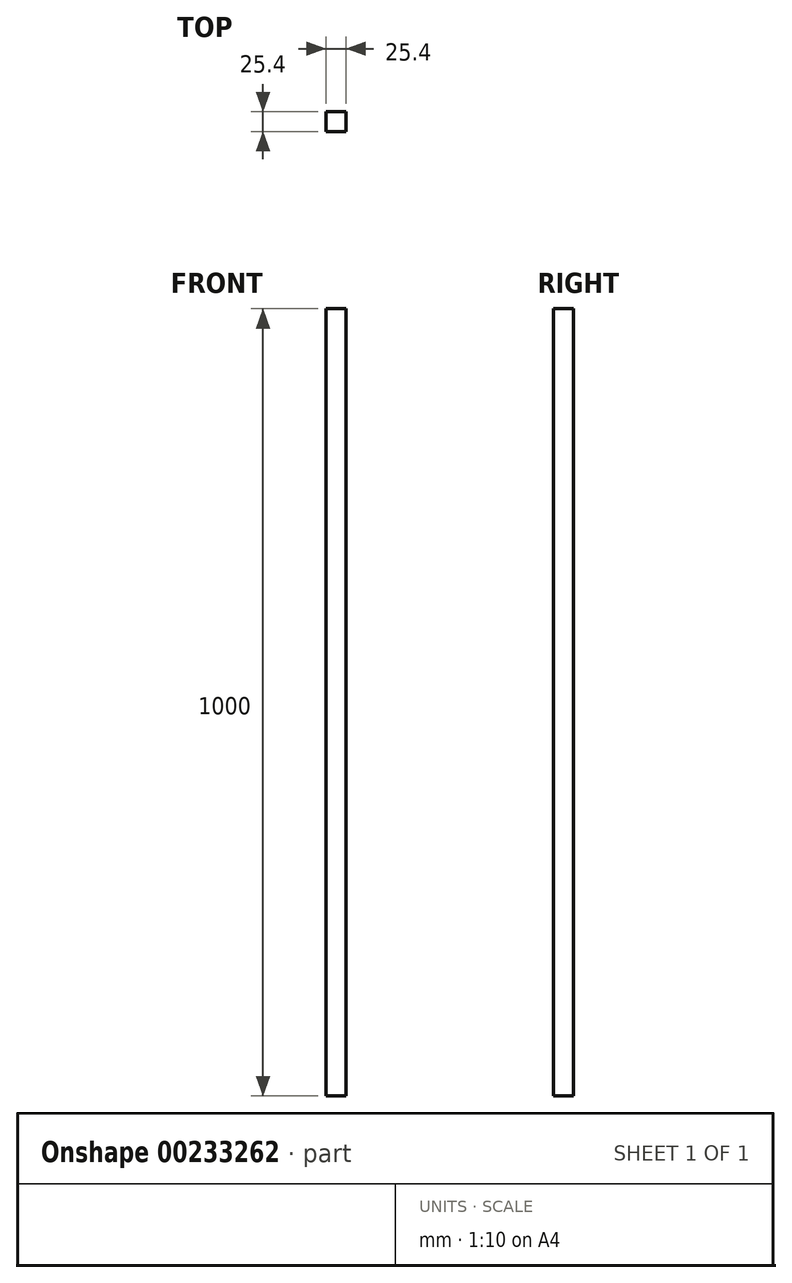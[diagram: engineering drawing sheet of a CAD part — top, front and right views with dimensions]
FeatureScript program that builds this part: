
annotation { "Feature Type Name" : "Feature", "Feature Type Description" : "" }
export const myFeature = defineFeature(function(context is Context, id is Id, definition is map)
    precondition{}
    {
        {
            var Q0;
            Q0=qCreatedBy(makeId("Top.planeOp"),FACE);
            var sketch = newSketch(context, id + "F0", { "sketchPlane" : qUnion([Q0])});
            skLineSegment(sketch, "E0.bottom", {"start": v(-35.9, 48.27) * mm, "end": v(-10.5, 48.27) * mm});
            skLineSegment(sketch, "E0.top", {"start": v(-35.9, 22.87) * mm, "end": v(-10.5, 22.87) * mm});
            skLineSegment(sketch, "E0.left", {"start": v(-35.9, 48.27) * mm, "end": v(-35.9, 22.87) * mm});
            skLineSegment(sketch, "E0.right", {"start": v(-10.5, 48.27) * mm, "end": v(-10.5, 22.87) * mm});
            skSolve(sketch);
        }
        {
            var Q0;
            Q0 = qSketchRegion(id + "F0", true);
            extrude(context, id + "F1", {"entities" : qUnion([Q0]), "depth" : 1000 * mm});
        }
    });
